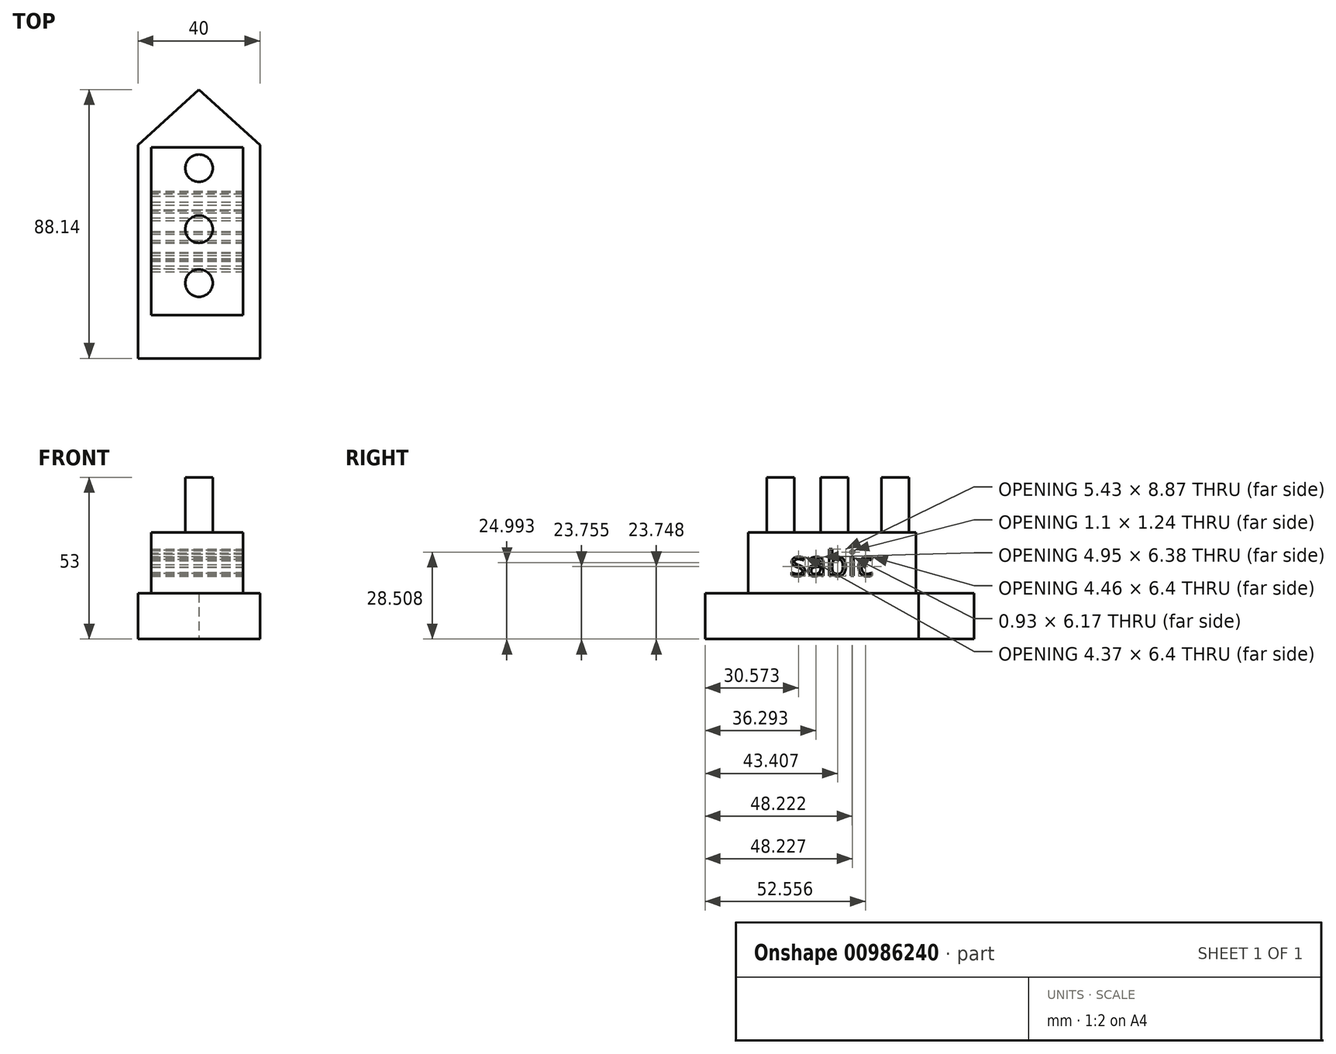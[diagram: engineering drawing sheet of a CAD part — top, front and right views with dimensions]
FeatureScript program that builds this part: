
annotation { "Feature Type Name" : "Feature", "Feature Type Description" : "" }
export const myFeature = defineFeature(function(context is Context, id is Id, definition is map)
    precondition{}
    {
        {
            var Q0;
            Q0=qCreatedBy(makeId("Top.planeOp"),FACE);
            var sketch = newSketch(context, id + "F0", { "sketchPlane" : qUnion([Q0])});
            skLineSegment(sketch, "E0", {"start": v(0, 38.14) * mm, "end": v(20, 20) * mm});
            skLineSegment(sketch, "E1", {"start": v(0, 38.14) * mm, "end": v(-20, 20) * mm});
            skLineSegment(sketch, "E2", {"start": v(-20, 20) * mm, "end": v(-20, -50) * mm});
            skLineSegment(sketch, "E3", {"start": v(-20, -50) * mm, "end": v(20, -50) * mm});
            skLineSegment(sketch, "E4", {"start": v(20, 20) * mm, "end": v(20, -50) * mm});
            skSolve(sketch);
        }
        {
            var Q0;
            Q0 = qSketchRegion(id + "F0", true);
            extrude(context, id + "F1", {"entities" : qUnion([Q0]), "depth" : 15 * mm, "offsetDistance" : 25 * mm});
        }
        {
            var Q0;
            Q0=makeQuery(id+"F1.opExtrude","CAP_FACE",FACE,{"disambiguationData":[OSD([sQuery(id+"F0.wireOp",EDGE,"E0"),sQuery(id+"F0.wireOp",EDGE,"E1"),sQuery(id+"F0.wireOp",EDGE,"E2"),sQuery(id+"F0.wireOp",EDGE,"E3"),sQuery(id+"F0.wireOp",EDGE,"E4")])],"isStart":false});
            var sketch = newSketch(context, id + "F2", { "sketchPlane" : qUnion([Q0])});
            skLineSegment(sketch, "E5.bottom", {"start": v(-15.62, 19.15) * mm, "end": v(14.38, 19.15) * mm});
            skLineSegment(sketch, "E5.top", {"start": v(-15.62, -35.85) * mm, "end": v(14.38, -35.85) * mm});
            skLineSegment(sketch, "E5.left", {"start": v(-15.62, 19.15) * mm, "end": v(-15.62, -35.85) * mm});
            skLineSegment(sketch, "E5.right", {"start": v(14.38, 19.15) * mm, "end": v(14.38, -35.85) * mm});
            skSolve(sketch);
        }
        {
            var Q0;
            Q0 = qSketchRegion(id + "F2", true);
            extrude(context, id + "F3", {"entities" : qUnion([Q0]), "operationType" : NewBodyOperationType.ADD, "depth" : 20 * mm, "offsetDistance" : 25 * mm});
        }
        {
            var Q0;
            Q0=makeQuery(id+"F3.opExtrude","CAP_FACE",FACE,{"disambiguationData":[OSD([sQuery(id+"F2.wireOp",EDGE,"E5.bottom"),sQuery(id+"F2.wireOp",EDGE,"E5.top"),sQuery(id+"F2.wireOp",EDGE,"E5.left"),sQuery(id+"F2.wireOp",EDGE,"E5.right")])],"isStart":false});
            var sketch = newSketch(context, id + "F4", { "sketchPlane" : qUnion([Q0])});
            skCircle(sketch, "E6", {"center": v(0, 12.36) * mm, "radius": 4.5 * mm});
            skCircle(sketch, "E7", {"center": v(0, -7.64) * mm, "radius": 4.5 * mm});
            skCircle(sketch, "E8", {"center": v(0, -25.3) * mm, "radius": 4.5 * mm});
            skSolve(sketch);
        }
        {
            var Q0;
            Q0 = qSketchRegion(id + "F4", true);
            extrude(context, id + "F5", {"entities" : qUnion([Q0]), "operationType" : NewBodyOperationType.ADD, "depth" : 18 * mm, "offsetDistance" : 25 * mm});
        }
        {
            var Q0;
            Q0=makeQuery(id+"F3.opExtrude","SWEPT_FACE",FACE,{"disambiguationData":[OSD([sQuery(id+"F2.wireOp",EDGE,"E5.right")])]});
            var sketch = newSketch(context, id + "F6", { "sketchPlane" : qUnion([Q0])});
            skText(sketch, "E9", { "text": "sabic\n", "fontName": "OpenSans-Regular.ttf"});
            const initialGuessF6  = {"E9": [-0.02221, 0.02067, 1, 0, 0.0083]};
            skSetInitialGuess(sketch, initialGuessF6);
            skSolve(sketch);
        }
        {
            var Q0;
            Q0 = qSketchRegion(id + "F6", true);
            extrude(context, id + "F7", {"entities" : qUnion([Q0]), "operationType" : NewBodyOperationType.REMOVE, "endBound" : BoundingType.THROUGH_ALL, "oppositeDirection" : true, "depth" : 5 * mm, "offsetDistance" : 25 * mm});
        }
    });
